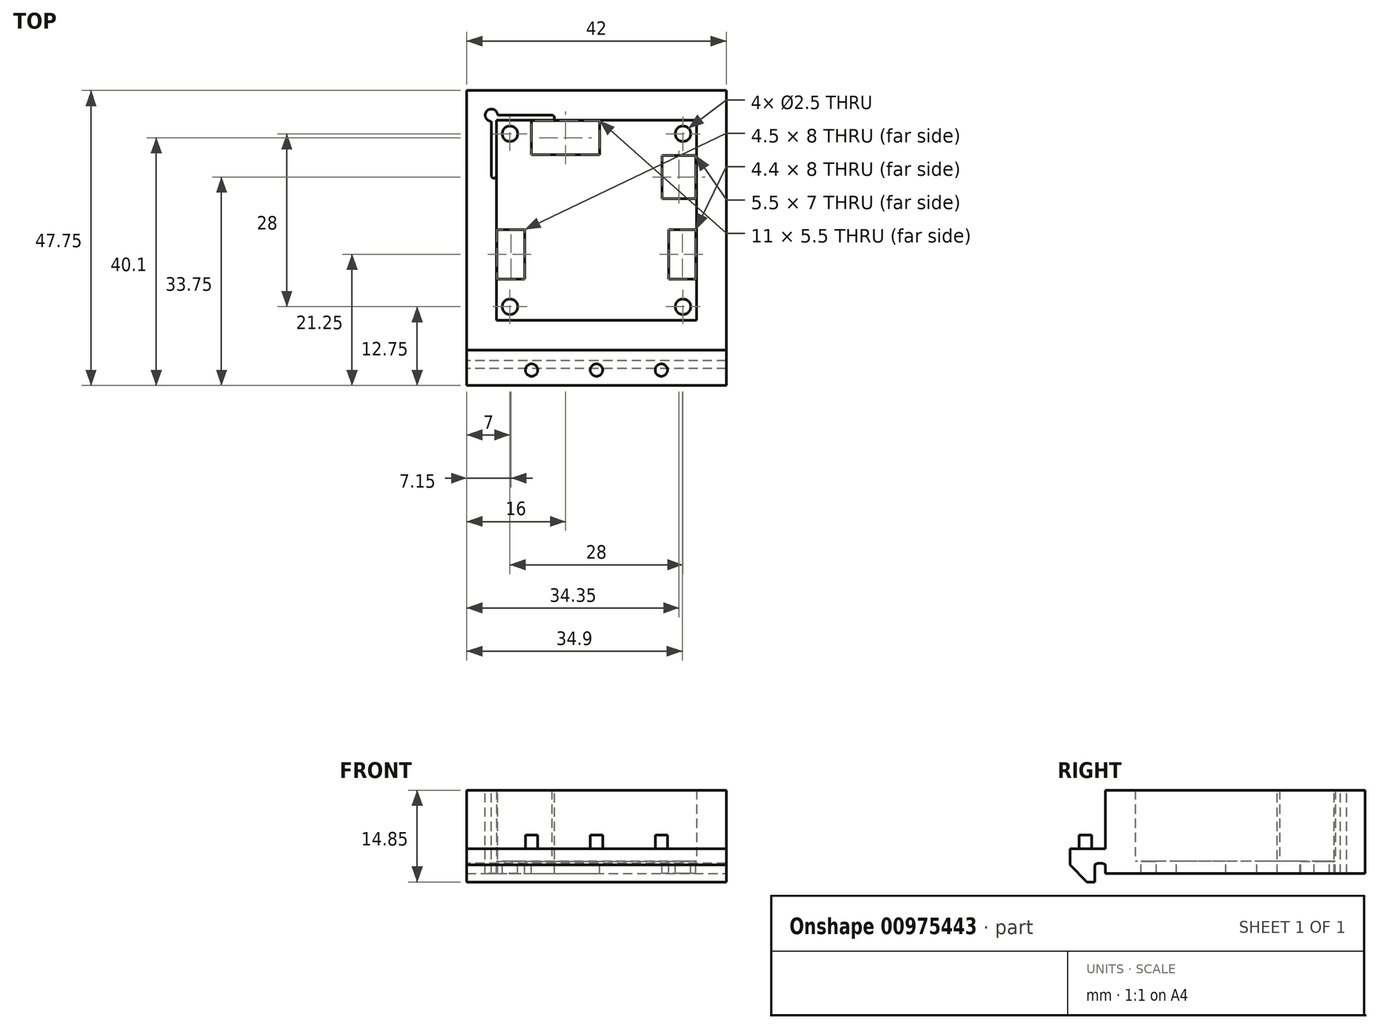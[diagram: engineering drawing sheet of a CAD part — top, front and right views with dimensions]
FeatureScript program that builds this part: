
annotation { "Feature Type Name" : "Feature", "Feature Type Description" : "" }
export const myFeature = defineFeature(function(context is Context, id is Id, definition is map)
    precondition{}
    {
        {
            var Q0;
            Q0=qCreatedBy(makeId("Top.planeOp"),FACE);
            var sketch = newSketch(context, id + "F0", { "sketchPlane" : qUnion([Q0])});
            skLineSegment(sketch, "E0.bottom", {"start": v(19, 19) * mm, "end": v(-19, 19) * mm, "construction": true});
            skLineSegment(sketch, "E0.top", {"start": v(19, -19) * mm, "end": v(2.62, -19) * mm, "construction": true});
            skLineSegment(sketch, "E0.left", {"start": v(19, 19) * mm, "end": v(19, -19) * mm, "construction": true});
            skLineSegment(sketch, "E0.right", {"start": v(-19, 19) * mm, "end": v(-19, -19) * mm, "construction": true});
            skPoint(sketch, "E0.middle", {"position": v(0, 0) * mm});
            skPoint(sketch, "E1", {"position": v(19, 0) * mm});
            skPoint(sketch, "E2", {"position": v(-19, 0) * mm});
            skPoint(sketch, "E3", {"position": v(0, 19) * mm});
            skPoint(sketch, "E4", {"position": v(0, -19) * mm});
            skPoint(sketch, "E5", {"position": v(17, 0) * mm});
            skPoint(sketch, "E6", {"position": v(-17, 0) * mm});
            skLineSegment(sketch, "E7", {"start": v(-19, 0) * mm, "end": v(-17, 0) * mm, "construction": true});
            skLineSegment(sketch, "E8", {"start": v(19, 0) * mm, "end": v(17, 0) * mm, "construction": true});
            skLineSegment(sketch, "E9", {"start": v(0, 19) * mm, "end": v(0, 17) * mm, "construction": true});
            skLineSegment(sketch, "E10", {"start": v(0, -17) * mm, "end": v(0, -19) * mm, "construction": true});
            skPoint(sketch, "E11", {"position": v(-16.2, 16.2) * mm});
            skPoint(sketch, "E12", {"position": v(16.2, -16.2) * mm});
            skPoint(sketch, "E13", {"position": v(16.2, 16.2) * mm});
            skPoint(sketch, "E14", {"position": v(-16.2, -16.2) * mm});
            skPoint(sketch, "E15", {"position": v(17, 4) * mm});
            skPoint(sketch, "E16", {"position": v(17, -4) * mm});
            skPoint(sketch, "E17", {"position": v(16.2, -4) * mm});
            skPoint(sketch, "E18", {"position": v(16.2, 4) * mm});
            skPoint(sketch, "E19", {"position": v(-17, 4) * mm});
            skPoint(sketch, "E20", {"position": v(-16.2, 4) * mm});
            skPoint(sketch, "E21", {"position": v(-17, -4) * mm});
            skPoint(sketch, "E22", {"position": v(-16.2, -4) * mm});
            skPoint(sketch, "E23", {"position": v(-4, 17) * mm});
            skPoint(sketch, "E24", {"position": v(-4, 16.2) * mm});
            skPoint(sketch, "E25", {"position": v(4, 17) * mm});
            skPoint(sketch, "E26", {"position": v(4, 16.2) * mm});
            skPoint(sketch, "E27", {"position": v(-4, -16.2) * mm});
            skPoint(sketch, "E28", {"position": v(4, -16.2) * mm});
            skPoint(sketch, "E29", {"position": v(-4, -17) * mm});
            skPoint(sketch, "E30", {"position": v(4, -17) * mm});
            skLineSegment(sketch, "E31", {"start": v(17, 4) * mm, "end": v(17, -4) * mm});
            skLineSegment(sketch, "E32", {"start": v(16.2, 4) * mm, "end": v(16.2, -4) * mm});
            skLineSegment(sketch, "E33", {"start": v(4, 16.2) * mm, "end": v(-4, 16.2) * mm});
            skLineSegment(sketch, "E34", {"start": v(-4, 17) * mm, "end": v(4, 17) * mm});
            skLineSegment(sketch, "E35", {"start": v(-16.2, 4) * mm, "end": v(-16.2, -4) * mm});
            skLineSegment(sketch, "E36", {"start": v(-17, -4) * mm, "end": v(-17, 4) * mm});
            skLineSegment(sketch, "E37", {"start": v(-4, -16.2) * mm, "end": v(4, -16.2) * mm});
            skLineSegment(sketch, "E38", {"start": v(4, -17) * mm, "end": v(-4, -17) * mm});
            skArc(sketch, "E39", {"start": v(16.2, 4) * mm, "mid": v(16.6, 4.4) * mm, "end": v(17, 4) * mm});
            skArc(sketch, "E40", {"start": v(17, -4) * mm, "mid": v(16.6, -4.4) * mm, "end": v(16.2, -4) * mm});
            skArc(sketch, "E41", {"start": v(4, -16.2) * mm, "mid": v(4.4, -16.6) * mm, "end": v(4, -17) * mm});
            skArc(sketch, "E42", {"start": v(-4, -16.2) * mm, "mid": v(-4.4, -16.6) * mm, "end": v(-4, -17) * mm});
            skArc(sketch, "E43", {"start": v(-17, -4) * mm, "mid": v(-16.6, -4.4) * mm, "end": v(-16.2, -4) * mm});
            skArc(sketch, "E44", {"start": v(-17, 4) * mm, "mid": v(-16.6, 4.4) * mm, "end": v(-16.2, 4) * mm});
            skArc(sketch, "E45", {"start": v(-4, 16.2) * mm, "mid": v(-4.4, 16.6) * mm, "end": v(-4, 17) * mm});
            skArc(sketch, "E46", {"start": v(4, 16.2) * mm, "mid": v(4.4, 16.6) * mm, "end": v(4, 17) * mm});
            skPoint(sketch, "E47", {"position": v(-7.2, 16.2) * mm});
            skPoint(sketch, "E48", {"position": v(-7.2, 17) * mm});
            skPoint(sketch, "E49", {"position": v(-16.2, 7.2) * mm});
            skPoint(sketch, "E50", {"position": v(-17, 7.2) * mm});
            skPoint(sketch, "E51", {"position": v(7.2, 16.2) * mm});
            skPoint(sketch, "E52", {"position": v(7.2, 17) * mm});
            skPoint(sketch, "E53", {"position": v(16.2, 7.2) * mm});
            skPoint(sketch, "E54", {"position": v(17, 7.2) * mm});
            skPoint(sketch, "E55", {"position": v(-17, -7.2) * mm});
            skPoint(sketch, "E56", {"position": v(-16.2, -7.2) * mm});
            skPoint(sketch, "E57", {"position": v(17, -7.2) * mm});
            skPoint(sketch, "E58", {"position": v(16.2, -7.2) * mm});
            skPoint(sketch, "E59", {"position": v(7.2, -17) * mm});
            skPoint(sketch, "E60", {"position": v(7.2, -16.2) * mm});
            skPoint(sketch, "E61", {"position": v(-7.2, -17) * mm});
            skPoint(sketch, "E62", {"position": v(-7.2, -16.2) * mm});
            skLineSegment(sketch, "E63", {"start": v(-7.2, 17) * mm, "end": v(-7.2, 16.2) * mm, "construction": true});
            skLineSegment(sketch, "E64", {"start": v(-17, 7.2) * mm, "end": v(-16.2, 7.2) * mm, "construction": true});
            skLineSegment(sketch, "E65", {"start": v(7.2, 17) * mm, "end": v(7.2, 16.2) * mm, "construction": true});
            skLineSegment(sketch, "E66", {"start": v(16.2, 7.2) * mm, "end": v(17, 7.2) * mm, "construction": true});
            skLineSegment(sketch, "E67", {"start": v(-17, -7.2) * mm, "end": v(-16.2, -7.2) * mm, "construction": true});
            skLineSegment(sketch, "E68", {"start": v(-7.2, -16.2) * mm, "end": v(-7.2, -17) * mm, "construction": true});
            skLineSegment(sketch, "E69", {"start": v(16.2, -7.2) * mm, "end": v(17, -7.2) * mm, "construction": true});
            skLineSegment(sketch, "E70", {"start": v(7.2, -16.2) * mm, "end": v(7.2, -17) * mm, "construction": true});
            skArc(sketch, "E71", {"start": v(-7.2, 17) * mm, "mid": v(-6.8, 16.6) * mm, "end": v(-7.2, 16.2) * mm});
            skArc(sketch, "E72", {"start": v(-16.2, 7.2) * mm, "mid": v(-16.6, 6.8) * mm, "end": v(-17, 7.2) * mm});
            skArc(sketch, "E73", {"start": v(7.2, 17) * mm, "mid": v(6.8, 16.6) * mm, "end": v(7.2, 16.2) * mm});
            skArc(sketch, "E74", {"start": v(17, 7.2) * mm, "mid": v(16.6, 6.8) * mm, "end": v(16.2, 7.2) * mm});
            skArc(sketch, "E75", {"start": v(-16.2, -7.2) * mm, "mid": v(-16.6, -6.8) * mm, "end": v(-17, -7.2) * mm});
            skArc(sketch, "E76", {"start": v(-7.2, -16.2) * mm, "mid": v(-6.8, -16.6) * mm, "end": v(-7.2, -17) * mm});
            skArc(sketch, "E77", {"start": v(7.2, -16.2) * mm, "mid": v(6.8, -16.6) * mm, "end": v(7.2, -17) * mm});
            skArc(sketch, "E78", {"start": v(17, -7.2) * mm, "mid": v(16.6, -6.8) * mm, "end": v(16.2, -7.2) * mm});
            skLineSegment(sketch, "E79", {"start": v(7.2, 17) * mm, "end": v(16.2, 17) * mm});
            skLineSegment(sketch, "E80", {"start": v(7.2, 16.2) * mm, "end": v(16.2, 16.2) * mm});
            skLineSegment(sketch, "E81", {"start": v(16.2, 7.2) * mm, "end": v(16.2, 16.2) * mm});
            skLineSegment(sketch, "E82", {"start": v(17, 16.2) * mm, "end": v(17, 7.2) * mm});
            skLineSegment(sketch, "E83", {"start": v(-16.2, 17) * mm, "end": v(-7.2, 17) * mm});
            skLineSegment(sketch, "E84", {"start": v(-16.2, 16.2) * mm, "end": v(-7.2, 16.2) * mm});
            skLineSegment(sketch, "E85", {"start": v(-16.2, 16.2) * mm, "end": v(-16.2, 7.2) * mm});
            skLineSegment(sketch, "E86", {"start": v(-16.2, -7.2) * mm, "end": v(-16.2, -16.2) * mm});
            skLineSegment(sketch, "E87", {"start": v(-7.2, -16.2) * mm, "end": v(-16.2, -16.2) * mm});
            skLineSegment(sketch, "E88", {"start": v(-17, -7.2) * mm, "end": v(-17, -16.2) * mm});
            skLineSegment(sketch, "E89", {"start": v(-16.2, -17) * mm, "end": v(-7.2, -17) * mm});
            skLineSegment(sketch, "E90", {"start": v(7.2, -17) * mm, "end": v(16.2, -17) * mm});
            skLineSegment(sketch, "E91", {"start": v(7.2, -16.2) * mm, "end": v(16.2, -16.2) * mm});
            skLineSegment(sketch, "E92", {"start": v(17, -16.2) * mm, "end": v(17, -7.2) * mm});
            skLineSegment(sketch, "E93", {"start": v(16.2, -7.2) * mm, "end": v(16.2, -16.2) * mm});
            skLineSegment(sketch, "E94", {"start": v(-17, 7.2) * mm, "end": v(-19, 7.2) * mm, "construction": true});
            skLineSegment(sketch, "E95", {"start": v(-17, -7.2) * mm, "end": v(-19, -7.2) * mm, "construction": true});
            skLineSegment(sketch, "E96", {"start": v(-7.2, 17) * mm, "end": v(-7.2, 19) * mm, "construction": true});
            skLineSegment(sketch, "E97", {"start": v(-7.2, -17) * mm, "end": v(-7.2, -19) * mm, "construction": true});
            skLineSegment(sketch, "E98", {"start": v(7.2, -17) * mm, "end": v(7.2, -19) * mm, "construction": true});
            skLineSegment(sketch, "E99", {"start": v(17, -7.2) * mm, "end": v(19, -7.2) * mm, "construction": true});
            skLineSegment(sketch, "E100", {"start": v(17, 7.2) * mm, "end": v(19, 7.2) * mm, "construction": true});
            skLineSegment(sketch, "E101", {"start": v(7.2, 17) * mm, "end": v(7.2, 19) * mm, "construction": true});
            skPoint(sketch, "E102", {"position": v(-11.7, 17) * mm});
            skPoint(sketch, "E103", {"position": v(-11.7, 16.2) * mm});
            skPoint(sketch, "E104", {"position": v(-17, 11.7) * mm});
            skPoint(sketch, "E105", {"position": v(-16.2, 11.7) * mm});
            skPoint(sketch, "E106", {"position": v(11.7, 17) * mm});
            skPoint(sketch, "E107", {"position": v(11.7, 16.2) * mm});
            skPoint(sketch, "E108", {"position": v(16.2, 11.7) * mm});
            skPoint(sketch, "E109", {"position": v(17, 11.7) * mm});
            skPoint(sketch, "E110", {"position": v(16.2, -11.7) * mm});
            skPoint(sketch, "E111", {"position": v(17, -11.7) * mm});
            skPoint(sketch, "E112", {"position": v(11.7, -16.2) * mm});
            skPoint(sketch, "E113", {"position": v(11.7, -17) * mm});
            skPoint(sketch, "E114", {"position": v(-11.7, -16.2) * mm});
            skPoint(sketch, "E115", {"position": v(-11.7, -17) * mm});
            skPoint(sketch, "E116", {"position": v(-16.2, -11.7) * mm});
            skPoint(sketch, "E117", {"position": v(-17, -11.7) * mm});
            skLineSegment(sketch, "E118", {"start": v(-17, 11.7) * mm, "end": v(-16.2, 11.7) * mm, "construction": true});
            skLineSegment(sketch, "E119", {"start": v(-11.7, 17) * mm, "end": v(-11.7, 16.2) * mm, "construction": true});
            skLineSegment(sketch, "E120", {"start": v(-11.7, -16.2) * mm, "end": v(-11.7, -17) * mm, "construction": true});
            skLineSegment(sketch, "E121", {"start": v(-16.2, -11.7) * mm, "end": v(-17, -11.7) * mm, "construction": true});
            skLineSegment(sketch, "E122", {"start": v(11.7, 17) * mm, "end": v(11.7, 16.2) * mm, "construction": true});
            skLineSegment(sketch, "E123", {"start": v(16.2, 11.7) * mm, "end": v(17, 11.7) * mm, "construction": true});
            skLineSegment(sketch, "E124", {"start": v(11.7, -17) * mm, "end": v(11.7, -16.2) * mm, "construction": true});
            skLineSegment(sketch, "E125", {"start": v(16.2, -11.7) * mm, "end": v(17, -11.7) * mm, "construction": true});
            skPoint(sketch, "E126", {"position": v(-14, 14) * mm});
            skLineSegment(sketch, "E127", {"start": v(-14, 19) * mm, "end": v(-14, 14) * mm, "construction": true});
            skLineSegment(sketch, "E128", {"start": v(-14, 14) * mm, "end": v(-19, 14) * mm, "construction": true});
            skPoint(sketch, "E129", {"position": v(-14, -14) * mm});
            skLineSegment(sketch, "E130", {"start": v(-19, -14) * mm, "end": v(-14, -14) * mm, "construction": true});
            skLineSegment(sketch, "E131", {"start": v(-14, -19) * mm, "end": v(-14, -14) * mm, "construction": true});
            skPoint(sketch, "E132", {"position": v(14, -14) * mm});
            skLineSegment(sketch, "E133", {"start": v(14, -19) * mm, "end": v(14, -14) * mm, "construction": true});
            skLineSegment(sketch, "E134", {"start": v(14, -14) * mm, "end": v(19, -14) * mm, "construction": true});
            skPoint(sketch, "E135", {"position": v(14, 14) * mm});
            skLineSegment(sketch, "E136", {"start": v(14, 19) * mm, "end": v(14, 14) * mm, "construction": true});
            skLineSegment(sketch, "E137", {"start": v(19, 14) * mm, "end": v(14, 14) * mm, "construction": true});
            skPoint(sketch, "E138", {"position": v(16.2, 0) * mm});
            skPoint(sketch, "E139", {"position": v(0, 16.2) * mm});
            skPoint(sketch, "E140", {"position": v(-16.2, 0) * mm});
            skPoint(sketch, "E141", {"position": v(0, -16.2) * mm});
            skLineSegment(sketch, "E142", {"start": v(16.2, 0) * mm, "end": v(17, 0) * mm, "construction": true});
            skLineSegment(sketch, "E143", {"start": v(0, 17) * mm, "end": v(0, 16.2) * mm, "construction": true});
            skLineSegment(sketch, "E144", {"start": v(0, -16.2) * mm, "end": v(0, -17) * mm, "construction": true});
            skLineSegment(sketch, "E145", {"start": v(-17, 0) * mm, "end": v(-16.2, 0) * mm, "construction": true});
            skLineSegment(sketch, "E146", {"start": v(17, 16.2) * mm, "end": v(17, 19) * mm, "construction": true});
            skPoint(sketch, "E147", {"position": v(-17, 17) * mm});
            skPoint(sketch, "E148", {"position": v(17, 17) * mm});
            skPoint(sketch, "E149", {"position": v(-17, -17) * mm});
            skPoint(sketch, "E150", {"position": v(17, -17) * mm});
            skLineSegment(sketch, "E151", {"start": v(16.2, -17) * mm, "end": v(17, -17) * mm, "construction": true});
            skLineSegment(sketch, "E152", {"start": v(17, -17) * mm, "end": v(17, -16.2) * mm, "construction": true});
            skLineSegment(sketch, "E153", {"start": v(17, 16.2) * mm, "end": v(17, 16.25) * mm});
            skPoint(sketch, "E154", {"position": v(-17, 16.2) * mm});
            skLineSegment(sketch, "E155", {"start": v(-16.2, 17) * mm, "end": v(-17, 17) * mm, "construction": true});
            skLineSegment(sketch, "E156", {"start": v(16.2, 4) * mm, "end": v(17, 4) * mm, "construction": true});
            skLineSegment(sketch, "E157", {"start": v(16.2, -4) * mm, "end": v(17, -4) * mm, "construction": true});
            skLineSegment(sketch, "E158", {"start": v(-4, 16.2) * mm, "end": v(-4, 17) * mm, "construction": true});
            skLineSegment(sketch, "E159", {"start": v(4, 16.2) * mm, "end": v(4, 17) * mm, "construction": true});
            skLineSegment(sketch, "E160", {"start": v(-16.2, 4) * mm, "end": v(-17, 4) * mm, "construction": true});
            skLineSegment(sketch, "E161", {"start": v(-16.2, -4) * mm, "end": v(-17, -4) * mm, "construction": true});
            skLineSegment(sketch, "E162", {"start": v(-4, -16.2) * mm, "end": v(-4, -17) * mm, "construction": true});
            skLineSegment(sketch, "E163", {"start": v(4, -16.2) * mm, "end": v(4, -17) * mm, "construction": true});
            skLineSegment(sketch, "E164", {"start": v(-7.2, 17) * mm, "end": v(-4, 17) * mm, "construction": true});
            skLineSegment(sketch, "E165", {"start": v(4, 17) * mm, "end": v(7.2, 17) * mm, "construction": true});
            skLineSegment(sketch, "E166", {"start": v(17, 7.2) * mm, "end": v(17, 4) * mm, "construction": true});
            skLineSegment(sketch, "E167", {"start": v(17, -7.2) * mm, "end": v(17, -4) * mm, "construction": true});
            skLineSegment(sketch, "E168", {"start": v(7.2, -17) * mm, "end": v(4, -17) * mm, "construction": true});
            skLineSegment(sketch, "E169", {"start": v(-4, -17) * mm, "end": v(-7.2, -17) * mm, "construction": true});
            skLineSegment(sketch, "E170", {"start": v(-17, -7.2) * mm, "end": v(-17, -4) * mm, "construction": true});
            skLineSegment(sketch, "E171", {"start": v(-17, 4) * mm, "end": v(-17, 7.2) * mm, "construction": true});
            skCircle(sketch, "E172", {"center": v(14, 14) * mm, "radius": 1.25 * mm});
            skPoint(sketch, "E173", {"position": v(14, 15.25) * mm});
            skPoint(sketch, "E174", {"position": v(15.25, 14) * mm});
            skPoint(sketch, "E175", {"position": v(16.2, 14) * mm});
            skPoint(sketch, "E176", {"position": v(14, 16.2) * mm});
            skCircle(sketch, "E177", {"center": v(-14, 14) * mm, "radius": 1.25 * mm});
            skPoint(sketch, "E178", {"position": v(-14, 15.25) * mm});
            skPoint(sketch, "E179", {"position": v(-15.25, 14) * mm});
            skCircle(sketch, "E180", {"center": v(-14, -14) * mm, "radius": 1.25 * mm});
            skCircle(sketch, "E181", {"center": v(14, -14) * mm, "radius": 1.25 * mm});
            skPoint(sketch, "E182", {"position": v(14, -15.25) * mm});
            skPoint(sketch, "E183", {"position": v(15.25, -14) * mm});
            skPoint(sketch, "E184", {"position": v(-15.25, -14) * mm});
            skPoint(sketch, "E185", {"position": v(-14, -15.25) * mm});
            skLineSegment(sketch, "E186", {"start": v(16.2, 7.2) * mm, "end": v(16.2, 4) * mm});
            skLineSegment(sketch, "E187", {"start": v(-7.2, 16.2) * mm, "end": v(-4, 16.2) * mm});
            skLineSegment(sketch, "E188", {"start": v(-7.2, -16.2) * mm, "end": v(-4, -16.2) * mm});
            skLineSegment(sketch, "E189", {"start": v(4, -16.2) * mm, "end": v(7.2, -16.2) * mm});
            skPoint(sketch, "E190", {"position": v(-16.2, -9) * mm});
            skPoint(sketch, "E191", {"position": v(-16.2, -2) * mm});
            skPoint(sketch, "E192", {"position": v(-16.2, 10) * mm});
            skPoint(sketch, "E193", {"position": v(10, 16.2) * mm});
            skPoint(sketch, "E194", {"position": v(16.2, -1.5) * mm});
            skPoint(sketch, "E195", {"position": v(16.2, -9.5) * mm});
            skPoint(sketch, "E196", {"position": v(10, 19) * mm});
            skPoint(sketch, "E197", {"position": v(-19, 10) * mm});
            skPoint(sketch, "E198", {"position": v(-19, 4) * mm});
            skPoint(sketch, "E199", {"position": v(-19, -2) * mm});
            skPoint(sketch, "E200", {"position": v(-19, -9) * mm});
            skPoint(sketch, "E201", {"position": v(19, -9) * mm});
            skPoint(sketch, "E202", {"position": v(19, -2) * mm});
            skLineSegment(sketch, "E203", {"start": v(0.5, 10.6) * mm, "end": v(0.5, 16.1) * mm});
            skLineSegment(sketch, "E204", {"start": v(-16.1, -9.5) * mm, "end": v(-11.6, -9.5) * mm});
            skLineSegment(sketch, "E205", {"start": v(-11.6, -9.5) * mm, "end": v(-11.6, -1.5) * mm});
            skLineSegment(sketch, "E206", {"start": v(-11.6, -1.5) * mm, "end": v(-16.1, -1.5) * mm});
            skLineSegment(sketch, "E207", {"start": v(16.1, -1.5) * mm, "end": v(11.7, -1.5) * mm});
            skLineSegment(sketch, "E208", {"start": v(11.7, -1.5) * mm, "end": v(11.7, -9.5) * mm});
            skLineSegment(sketch, "E209", {"start": v(11.7, -9.5) * mm, "end": v(16.1, -9.5) * mm});
            skPoint(sketch, "E210", {"position": v(-2.62, -19) * mm});
            skPoint(sketch, "E211", {"position": v(2.62, -19) * mm});
            skLineSegment(sketch, "E212.trimOffspring", {"start": v(-2.62, -19) * mm, "end": v(-19, -19) * mm, "construction": true});
            skLineSegment(sketch, "E213.bottom", {"start": v(-21, -21) * mm, "end": v(21, -21) * mm});
            skLineSegment(sketch, "E213.top", {"start": v(-21, 21) * mm, "end": v(21, 21) * mm});
            skLineSegment(sketch, "E213.left", {"start": v(-21, -21) * mm, "end": v(-21, 21) * mm});
            skLineSegment(sketch, "E213.right", {"start": v(21, -21) * mm, "end": v(21, 21) * mm});
            skPoint(sketch, "E214", {"position": v(2.62, -21) * mm});
            skPoint(sketch, "E215", {"position": v(-2.62, -21) * mm});
            skLineSegment(sketch, "E216", {"start": v(-2.62, -21) * mm, "end": v(-2.62, -19) * mm, "construction": true});
            skLineSegment(sketch, "E217", {"start": v(-16.1, -1.5) * mm, "end": v(-16.1, -9.5) * mm});
            skLineSegment(sketch, "E218", {"start": v(16.1, -1.5) * mm, "end": v(16.1, -9.5) * mm});
            skLineSegment(sketch, "E219", {"start": v(-10.5, 10.6) * mm, "end": v(-10.5, 16.1) * mm});
            skLineSegment(sketch, "E220", {"start": v(-10.5, 16.1) * mm, "end": v(0.5, 16.1) * mm});
            skLineSegment(sketch, "E221", {"start": v(-10.5, 10.6) * mm, "end": v(0.5, 10.6) * mm});
            skPoint(sketch, "E222", {"position": v(10.6, 10.5) * mm});
            skPoint(sketch, "E223", {"position": v(10.6, 3.5) * mm});
            skLineSegment(sketch, "E224", {"start": v(10.6, 3.5) * mm, "end": v(10.6, 10.5) * mm});
            skLineSegment(sketch, "E225", {"start": v(16.1, 10.5) * mm, "end": v(16.1, 3.5) * mm});
            skLineSegment(sketch, "E226", {"start": v(16.1, 3.5) * mm, "end": v(10.6, 3.5) * mm});
            skLineSegment(sketch, "E227", {"start": v(10.6, 10.5) * mm, "end": v(16.1, 10.5) * mm});
            skLineSegment(sketch, "E228", {"start": v(16.2, 17) * mm, "end": v(19, 17) * mm, "construction": true});
            skLineSegment(sketch, "E229", {"start": v(17, -17) * mm, "end": v(19, -17) * mm, "construction": true});
            skLineSegment(sketch, "E230", {"start": v(17, -17) * mm, "end": v(17, -19) * mm, "construction": true});
            skLineSegment(sketch, "E231", {"start": v(-17, 16.2) * mm, "end": v(-17, 17) * mm, "construction": true});
            skLineSegment(sketch, "E232", {"start": v(-17, 16.2) * mm, "end": v(-17, 7.2) * mm});
            skLineSegment(sketch, "E233", {"start": v(-17, 17) * mm, "end": v(-17, 19) * mm, "construction": true});
            skLineSegment(sketch, "E234", {"start": v(-19, 17) * mm, "end": v(-17, 17) * mm, "construction": true});
            skLineSegment(sketch, "E235", {"start": v(-17, -16.2) * mm, "end": v(-17, -17) * mm, "construction": true});
            skLineSegment(sketch, "E236", {"start": v(-16.2, -17) * mm, "end": v(-17, -17) * mm, "construction": true});
            skLineSegment(sketch, "E237", {"start": v(-17, -17) * mm, "end": v(-19, -17) * mm, "construction": true});
            skLineSegment(sketch, "E238", {"start": v(-17, -17) * mm, "end": v(-17, -19) * mm, "construction": true});
            skArc(sketch, "E239", {"start": v(16, -17) * mm, "mid": v(17.7, -17.7) * mm, "end": v(17, -16) * mm});
            skArc(sketch, "E240", {"start": v(-16, 17) * mm, "mid": v(-17.7, 17.7) * mm, "end": v(-17, 16) * mm});
            skArc(sketch, "E241", {"start": v(17, 16) * mm, "mid": v(17.7, 17.7) * mm, "end": v(16, 17) * mm});
            skArc(sketch, "E242", {"start": v(-17, -16) * mm, "mid": v(-17.7, -17.7) * mm, "end": v(-16, -17) * mm});
            skPoint(sketch, "E243", {"position": v(16, 17) * mm});
            skPoint(sketch, "E244", {"position": v(17, 16) * mm});
            skPoint(sketch, "E245", {"position": v(-17, 16) * mm});
            skPoint(sketch, "E246", {"position": v(-16, 17) * mm});
            skPoint(sketch, "E247", {"position": v(-17, -16) * mm});
            skPoint(sketch, "E248", {"position": v(-16, -17) * mm});
            skPoint(sketch, "E249", {"position": v(17, -16) * mm});
            skPoint(sketch, "E250", {"position": v(16, -17) * mm});
            skLineSegment(sketch, "E251", {"start": v(4, 16.2) * mm, "end": v(7.2, 16.2) * mm});
            skLineSegment(sketch, "E252", {"start": v(-16.2, 7.2) * mm, "end": v(-16.2, 4) * mm});
            skLineSegment(sketch, "E253", {"start": v(-16.2, -7.2) * mm, "end": v(-16.2, -4) * mm});
            skLineSegment(sketch, "E254", {"start": v(16.2, -7.2) * mm, "end": v(16.2, -4) * mm});
            skPoint(sketch, "E255", {"position": v(-16.1, -5.5) * mm});
            skPoint(sketch, "E256", {"position": v(-11.6, -5.5) * mm});
            skLineSegment(sketch, "E257", {"start": v(-19, -2) * mm, "end": v(-19, -9) * mm, "construction": true});
            skPoint(sketch, "E258", {"position": v(-19, -5.5) * mm});
            skPoint(sketch, "E259", {"position": v(-10.5, 13.35) * mm});
            skPoint(sketch, "E260", {"position": v(19, 10) * mm});
            skPoint(sketch, "E261", {"position": v(19, 4) * mm});
            skLineSegment(sketch, "E262", {"start": v(19, 10) * mm, "end": v(19, 4) * mm, "construction": true});
            skPoint(sketch, "E263", {"position": v(19, 7) * mm});
            skPoint(sketch, "E264", {"position": v(-10, 19) * mm});
            skLineSegment(sketch, "E265", {"start": v(-10, 19) * mm, "end": v(0, 19) * mm, "construction": true});
            skPoint(sketch, "E266", {"position": v(-5, 19) * mm});
            skPoint(sketch, "E267", {"position": v(-5, 16.1) * mm});
            skPoint(sketch, "E268", {"position": v(16.1, 7) * mm});
            skPoint(sketch, "E269", {"position": v(16.1, -5.5) * mm});
            skLineSegment(sketch, "E270", {"start": v(19, -2) * mm, "end": v(19, -9) * mm, "construction": true});
            skPoint(sketch, "E271", {"position": v(19, -5.5) * mm});
            skSolve(sketch);
        }
        {
            var Q0;
            Q0=qCreatedBy(makeId("Right.planeOp"),FACE);
            var sketch = newSketch(context, id + "F1", { "sketchPlane" : qUnion([Q0])});
            skPoint(sketch, "E272", {"position": v(-21, 0) * mm});
            skPoint(sketch, "E273", {"position": v(-21, -2.6) * mm});
            skLineSegment(sketch, "E274", {"start": v(-21, 0) * mm, "end": v(-22.75, 0) * mm});
            skLineSegment(sketch, "E275", {"start": v(-22.75, -2.6) * mm, "end": v(-21, -2.6) * mm, "construction": true});
            skLineSegment(sketch, "E276", {"start": v(-21, 0) * mm, "end": v(-21, -2.6) * mm});
            skLineSegment(sketch, "E277", {"start": v(-22.75, -2.6) * mm, "end": v(-22.75, -5.35) * mm});
            skLineSegment(sketch, "E278", {"start": v(-22.75, -5.35) * mm, "end": v(-24, -5.35) * mm});
            skLineSegment(sketch, "E279", {"start": v(-24, -5.35) * mm, "end": v(-26.75, -2.6) * mm});
            skLineSegment(sketch, "E280", {"start": v(-26.75, -2.6) * mm, "end": v(-26.75, 0) * mm});
            skLineSegment(sketch, "E281", {"start": v(-26.75, 0) * mm, "end": v(-22.75, 0) * mm});
            skArc(sketch, "E282", {"start": v(-21, -2.6) * mm, "mid": v(-21.87, -2.32) * mm, "end": v(-22.75, -2.6) * mm});
            skSolve(sketch);
        }
        {
            var Q0;
            Q0=qSketchRegion(id+"F0",true);
            var Q1;
            Q1=makeQuery(id+"F0.imprint","IMPRINT",FACE,{"disambiguationData":[TD([[makeQuery(id+"F0.imprint","IMPRINT",EDGE,{"derivedFrom":sQuery(id+"F0.wireOp",EDGE,"E31")}),1.0]])]});
            var Q2;
            Q2=makeQuery(id+"F0.imprint","IMPRINT",FACE,{"disambiguationData":[TD([[makeQuery(id+"F0.imprint","IMPRINT",EDGE,{"derivedFrom":sQuery(id+"F0.wireOp",EDGE,"E33")}),-1.0]])]});
            var Q3;
            Q3=makeQuery(id+"F0.imprint","IMPRINT",FACE,{"disambiguationData":[TD([[makeQuery(id+"F0.imprint","IMPRINT",EDGE,{"derivedFrom":sQuery(id+"F0.wireOp",EDGE,"E73")}),1.0]])]});
            var Q4;
            Q4=makeQuery(id+"F0.imprint","IMPRINT",FACE,{"disambiguationData":[TD([[makeQuery(id+"F0.imprint","IMPRINT",EDGE,{"derivedFrom":sQuery(id+"F0.wireOp",EDGE,"E71")}),-1.0]])]});
            var Q5;
            Q5=makeQuery(id+"F0.imprint","IMPRINT",FACE,{"disambiguationData":[TD([[makeQuery(id+"F0.imprint","IMPRINT",EDGE,{"derivedFrom":sQuery(id+"F0.wireOp",EDGE,"E35")}),-1.0]])]});
            var Q6;
            Q6=makeQuery(id+"F0.imprint","IMPRINT",FACE,{"disambiguationData":[TD([[makeQuery(id+"F0.imprint","IMPRINT",EDGE,{"derivedFrom":sQuery(id+"F0.wireOp",EDGE,"E31")}),-1.0]])]});
            var Q7;
            Q7=makeQuery(id+"F0.imprint","IMPRINT",FACE,{"disambiguationData":[TD([[makeQuery(id+"F0.imprint","IMPRINT",EDGE,{"derivedFrom":sQuery(id+"F0.wireOp",EDGE,"E77")}),1.0]])]});
            var Q8;
            Q8=makeQuery(id+"F0.imprint","IMPRINT",FACE,{"disambiguationData":[TD([[makeQuery(id+"F0.imprint","IMPRINT",EDGE,{"derivedFrom":sQuery(id+"F0.wireOp",EDGE,"E75")}),1.0]])]});
            var Q9;
            Q9=makeQuery(id+"F0.imprint","IMPRINT",FACE,{"disambiguationData":[TD([[makeQuery(id+"F0.imprint","IMPRINT",EDGE,{"derivedFrom":sQuery(id+"F0.wireOp",EDGE,"E37")}),-1.0]])]});
            var Q10;
            Q10=makeQuery(id+"F0.imprint","IMPRINT",FACE,{"disambiguationData":[TD([[makeQuery(id+"F0.imprint","IMPRINT",EDGE,{"derivedFrom":sQuery(id+"F0.wireOp",EDGE,"E32")}),-1.0]])]});
            extrude(context, id + "F2", {"entities" : qUnion([Q0, Q1, Q2, Q3, Q4, Q5, Q6, Q7, Q8, Q9, Q10]), "oppositeDirection" : true, "depth" : 4 * mm, "offsetDistance" : 25 * mm});
        }
        {
            var Q0;
            Q0=makeQuery(id+"F1.imprint","IMPRINT",FACE,{"disambiguationData":[TD([[makeQuery(id+"F1.imprint","IMPRINT",EDGE,{"derivedFrom":sQuery(id+"F1.wireOp",EDGE,"E274")}),1.0]])]});
            extrude(context, id + "F3", {"entities" : qUnion([Q0]), "operationType" : NewBodyOperationType.ADD, "depth" : 21 * mm, "offsetDistance" : 25 * mm});
        }
        {
            var Q0;
            Q0=makeQuery(id+"F3.opExtrude","CAP_FACE",FACE,{"disambiguationData":[OSD([sQuery(id+"F1.wireOp",EDGE,"E274"),sQuery(id+"F1.wireOp",EDGE,"E275"),sQuery(id+"F1.wireOp",EDGE,"E276"),sQuery(id+"F1.wireOp",EDGE,"E277"),sQuery(id+"F1.wireOp",EDGE,"E278"),sQuery(id+"F1.wireOp",EDGE,"E279"),sQuery(id+"F1.wireOp",EDGE,"E280"),sQuery(id+"F1.wireOp",EDGE,"E281")])],"isStart":true});
            extrude(context, id + "F4", {"entities" : qUnion([Q0]), "operationType" : NewBodyOperationType.ADD, "depth" : 21 * mm, "offsetDistance" : 25 * mm});
        }
        {
            var Q0;
            Q0=makeQuery(id+"F0.imprint","IMPRINT",FACE,{"disambiguationData":[TD([[makeQuery(id+"F0.imprint","IMPRINT",EDGE,{"derivedFrom":sQuery(id+"F0.wireOp",EDGE,"E71")}),-1.0]])]});
            var Q1;
            Q1=makeQuery(id+"F0.imprint","IMPRINT",FACE,{"disambiguationData":[TD([[makeQuery(id+"F0.imprint","IMPRINT",EDGE,{"derivedFrom":sQuery(id+"F0.wireOp",EDGE,"E35")}),-1.0]])]});
            var Q2;
            Q2=makeQuery(id+"F0.imprint","IMPRINT",FACE,{"disambiguationData":[TD([[makeQuery(id+"F0.imprint","IMPRINT",EDGE,{"derivedFrom":sQuery(id+"F0.wireOp",EDGE,"E75")}),1.0]])]});
            var Q3;
            Q3=makeQuery(id+"F0.imprint","IMPRINT",FACE,{"disambiguationData":[TD([[makeQuery(id+"F0.imprint","IMPRINT",EDGE,{"derivedFrom":sQuery(id+"F0.wireOp",EDGE,"E33")}),-1.0]])]});
            var Q4;
            Q4=makeQuery(id+"F0.imprint","IMPRINT",FACE,{"disambiguationData":[TD([[makeQuery(id+"F0.imprint","IMPRINT",EDGE,{"derivedFrom":sQuery(id+"F0.wireOp",EDGE,"E73")}),1.0]])]});
            var Q5;
            Q5=makeQuery(id+"F0.imprint","IMPRINT",FACE,{"disambiguationData":[TD([[makeQuery(id+"F0.imprint","IMPRINT",EDGE,{"derivedFrom":sQuery(id+"F0.wireOp",EDGE,"E31")}),-1.0]])]});
            var Q6;
            Q6=makeQuery(id+"F0.imprint","IMPRINT",FACE,{"disambiguationData":[TD([[makeQuery(id+"F0.imprint","IMPRINT",EDGE,{"derivedFrom":sQuery(id+"F0.wireOp",EDGE,"E37")}),-1.0]])]});
            var Q7;
            Q7=makeQuery(id+"F0.imprint","IMPRINT",FACE,{"disambiguationData":[TD([[makeQuery(id+"F0.imprint","IMPRINT",EDGE,{"derivedFrom":sQuery(id+"F0.wireOp",EDGE,"E77")}),1.0]])]});
            extrude(context, id + "F5", {"entities" : qUnion([Q0, Q1, Q2, Q3, Q4, Q5, Q6, Q7]), "operationType" : NewBodyOperationType.ADD, "depth" : 9.5 * mm, "offsetDistance" : 25 * mm});
        }
        {
            var Q0;
            {var subQ0=sQuery(id+"F1.wireOp",EDGE,"E281");var subQ1=sQuery(id+"F1.wireOp",EDGE,"E274");Q0=makeQuery(id+"F4.boolean.opBoolean","MERGE",FACE,{"derivedFrom":[makeQuery(id+"F3.boolean.opBoolean","MERGE",FACE,{"derivedFrom":[makeQuery(id+"F2.opExtrude","CAP_FACE",FACE,{"disambiguationData":[OSD([sQuery(id+"F0.wireOp",EDGE,"E172"),sQuery(id+"F0.wireOp",EDGE,"E177"),sQuery(id+"F0.wireOp",EDGE,"E180"),sQuery(id+"F0.wireOp",EDGE,"E181"),sQuery(id+"F0.wireOp",EDGE,"E203"),sQuery(id+"F0.wireOp",EDGE,"E204"),sQuery(id+"F0.wireOp",EDGE,"E205"),sQuery(id+"F0.wireOp",EDGE,"E206"),sQuery(id+"F0.wireOp",EDGE,"E207"),sQuery(id+"F0.wireOp",EDGE,"E208"),sQuery(id+"F0.wireOp",EDGE,"E209"),sQuery(id+"F0.wireOp",EDGE,"E213.bottom"),sQuery(id+"F0.wireOp",EDGE,"E213.top"),sQuery(id+"F0.wireOp",EDGE,"E213.left"),sQuery(id+"F0.wireOp",EDGE,"E213.right"),sQuery(id+"F0.wireOp",EDGE,"E217"),sQuery(id+"F0.wireOp",EDGE,"E218"),sQuery(id+"F0.wireOp",EDGE,"E219"),sQuery(id+"F0.wireOp",EDGE,"E220"),sQuery(id+"F0.wireOp",EDGE,"E221"),sQuery(id+"F0.wireOp",EDGE,"E224"),sQuery(id+"F0.wireOp",EDGE,"E225"),sQuery(id+"F0.wireOp",EDGE,"E226"),sQuery(id+"F0.wireOp",EDGE,"E227")])],"isStart":true}),makeQuery(id+"F3.opExtrude","SWEPT_FACE",FACE,{"disambiguationData":[OSD([subQ1,subQ0])]})]}),makeQuery(id+"F4.opExtrude","SWEPT_FACE",FACE,{"disambiguationData":[OSD([subQ1,subQ0])]})]});}
            var sketch = newSketch(context, id + "F6", { "sketchPlane" : qUnion([Q0])});
            skPoint(sketch, "E283", {"position": v(0, -17) * mm});
            skPoint(sketch, "E284", {"position": v(0, -18.5) * mm});
            skPoint(sketch, "E285", {"position": v(0, -20.5) * mm});
            skLineSegment(sketch, "E286", {"start": v(0, -20.5) * mm, "end": v(21, -20.5) * mm, "construction": true});
            skLineSegment(sketch, "E287", {"start": v(0, -20.5) * mm, "end": v(-21, -20.5) * mm, "construction": true});
            skLineSegment(sketch, "E288", {"start": v(0, -20.5) * mm, "end": v(0, -24.25) * mm, "construction": true});
            skLineSegment(sketch, "E289", {"start": v(-10.5, -20.5) * mm, "end": v(-10.5, -24.25) * mm, "construction": true});
            skLineSegment(sketch, "E290", {"start": v(10.5, -20.5) * mm, "end": v(10.5, -24.25) * mm, "construction": true});
            skCircle(sketch, "E291", {"center": v(-10.5, -24.25) * mm, "radius": 1 * mm});
            skCircle(sketch, "E292", {"center": v(0, -24.25) * mm, "radius": 1 * mm});
            skCircle(sketch, "E293", {"center": v(10.5, -24.25) * mm, "radius": 1 * mm});
            skLineSegment(sketch, "E294.trimOffspring", {"start": v(-10.5, -25.25) * mm, "end": v(-10.5, -26.75) * mm, "construction": true});
            skLineSegment(sketch, "E295.trimOffspring", {"start": v(0, -25.25) * mm, "end": v(0, -26.75) * mm, "construction": true});
            skLineSegment(sketch, "E296.trimOffspring", {"start": v(10.5, -25.25) * mm, "end": v(10.5, -26.75) * mm, "construction": true});
            skSolve(sketch);
        }
        {
            var Q0;
            Q0=qSketchRegion(id+"F6",true);
            extrude(context, id + "F7", {"entities" : qUnion([Q0]), "operationType" : NewBodyOperationType.ADD, "depth" : 2.25 * mm, "offsetDistance" : 25 * mm});
        }
        {
            var Q0;
            Q0=makeQuery(id+"F0.imprint","IMPRINT",FACE,{"disambiguationData":[TD([[makeQuery(id+"F0.imprint","IMPRINT",EDGE,{"derivedFrom":sQuery(id+"F0.wireOp",EDGE,"E32")}),-1.0]])]});
            extrude(context, id + "F8", {"entities" : qUnion([Q0]), "operationType" : NewBodyOperationType.REMOVE, "oppositeDirection" : true, "depth" : 2 * mm, "offsetDistance" : 25 * mm});
        }
    });
